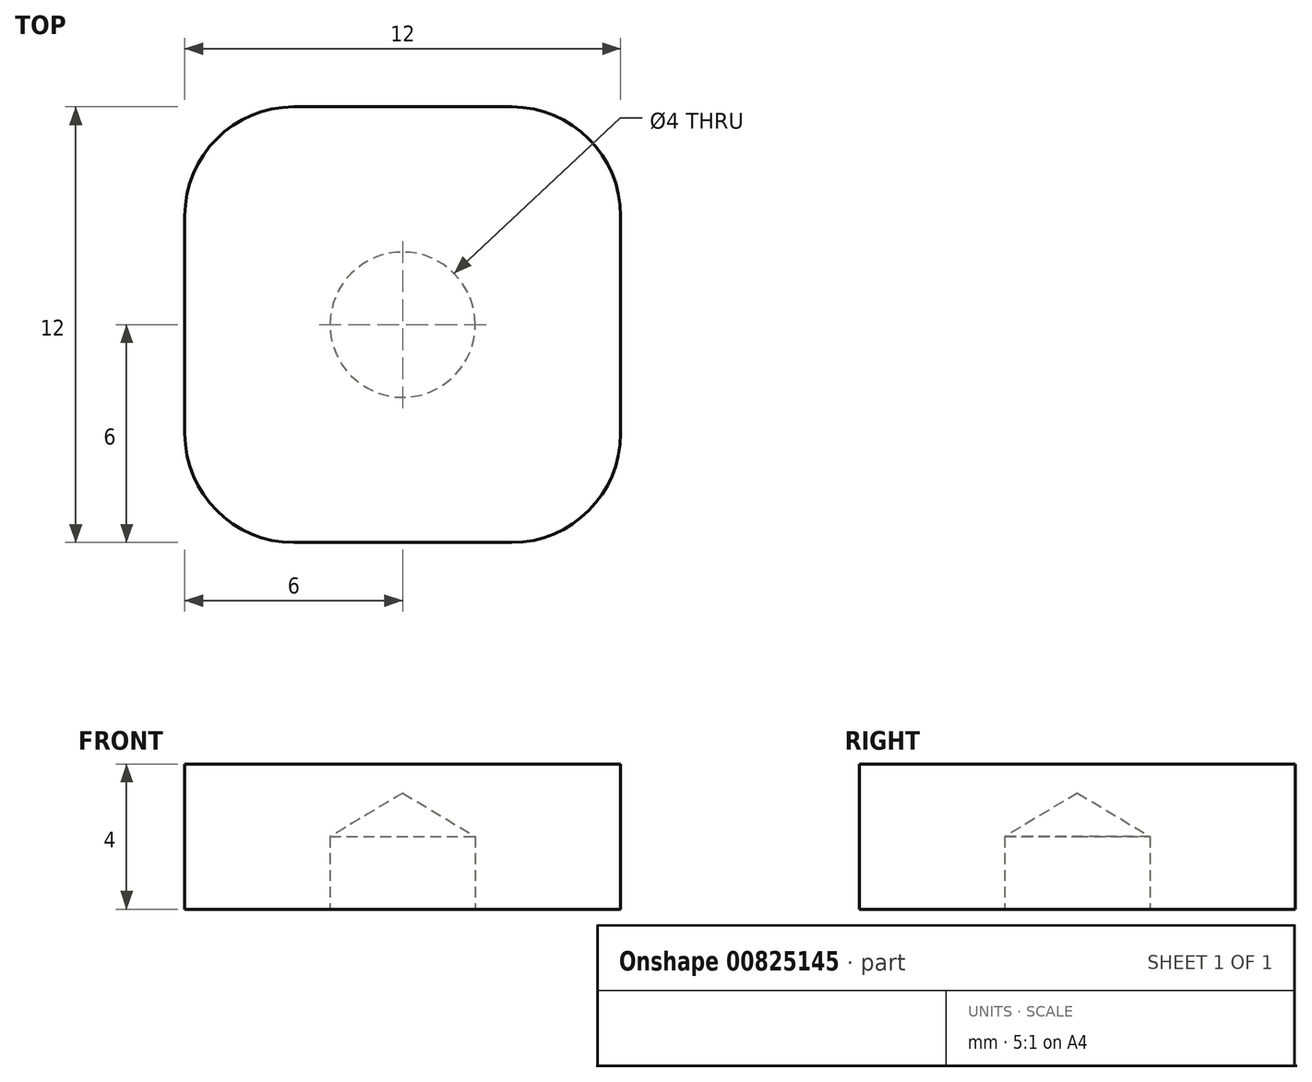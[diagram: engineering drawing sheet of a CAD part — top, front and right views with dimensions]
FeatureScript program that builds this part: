
annotation { "Feature Type Name" : "Feature", "Feature Type Description" : "" }
export const myFeature = defineFeature(function(context is Context, id is Id, definition is map)
    precondition{}
    {
        {
            var Q0;
            Q0=qCreatedBy(makeId("Top.planeOp"),FACE);
            var sketch = newSketch(context, id + "F0", { "sketchPlane" : qUnion([Q0])});
            skLineSegment(sketch, "E0.bottom", {"start": v(-6, 6) * mm, "end": v(6, 6) * mm});
            skLineSegment(sketch, "E0.top", {"start": v(-6, -6) * mm, "end": v(6, -6) * mm});
            skLineSegment(sketch, "E0.left", {"start": v(-6, 6) * mm, "end": v(-6, -6) * mm});
            skLineSegment(sketch, "E0.right", {"start": v(6, 6) * mm, "end": v(6, -6) * mm});
            skPoint(sketch, "E0.middle", {"position": v(0, 0) * mm});
            skLineSegment(sketch, "E1", {"start": v(6, 6) * mm, "end": v(-6, -6) * mm, "construction": true});
            skLineSegment(sketch, "E2", {"start": v(6, -6) * mm, "end": v(-6, 6) * mm, "construction": true});
            skSolve(sketch);
        }
        {
            var Q0;
            Q0=makeQuery(id+"F0.imprint","IMPRINT",FACE,{"disambiguationData":[TD([[makeQuery(id+"F0.imprint","IMPRINT",EDGE,{"derivedFrom":sQuery(id+"F0.wireOp",EDGE,"E0.bottom")}),-1.0]])]});
            extrude(context, id + "F1", {"entities" : qUnion([Q0]), "depth" : 4 * mm, "offsetDistance" : 25 * mm});
        }
        {
            var Q0;
            Q0=sQuery(id+"F0.wireOp",VERTEX,"E0.middle");
            var Q1;
            Q1=makeQuery(id+"F1.opExtrude","SWEPT_BODY",BODY,{"disambiguationData":[OSD([sQuery(id+"F0.wireOp",EDGE,"E0.bottom"),sQuery(id+"F0.wireOp",EDGE,"E0.top"),sQuery(id+"F0.wireOp",EDGE,"E0.left"),sQuery(id+"F0.wireOp",EDGE,"E0.right")])]});
            hole(context, id + "F2", {"style" : HoleStyle.SIMPLE, "endStyle" : HoleEndStyle.BLIND, "oppositeDirection" : true, "holeDiameter" : 4 * mm, "majorDiameter" : 5 * mm, "holeDepth" : 2 * mm, "isTappedThrough" : true, "tappedDepth" : 12 * mm, "tapClearance" : 3, "startFromSketch" : true, "locations" : qUnion([Q0]), "scope" : qUnion([Q1])});
        }
        {
            var Q0;
            Q0=makeQuery(id+"F1.opExtrude","SWEPT_EDGE",EDGE,{"disambiguationData":[OSD([sQuery(id+"F0.wireOp",EDGE,"E0.bottom"),sQuery(id+"F0.wireOp",EDGE,"E0.right")])]});
            var Q1;
            Q1=makeQuery(id+"F1.opExtrude","SWEPT_EDGE",EDGE,{"disambiguationData":[OSD([sQuery(id+"F0.wireOp",EDGE,"E0.bottom"),sQuery(id+"F0.wireOp",EDGE,"E0.left")])]});
            var Q2;
            Q2=makeQuery(id+"F1.opExtrude","SWEPT_EDGE",EDGE,{"disambiguationData":[OSD([sQuery(id+"F0.wireOp",EDGE,"E0.top"),sQuery(id+"F0.wireOp",EDGE,"E0.left")])]});
            var Q3;
            Q3=makeQuery(id+"F1.opExtrude","SWEPT_EDGE",EDGE,{"disambiguationData":[OSD([sQuery(id+"F0.wireOp",EDGE,"E0.top"),sQuery(id+"F0.wireOp",EDGE,"E0.right")])]});
            fillet(context, id + "F3", {"entities" : qUnion([Q0, Q1, Q2, Q3]), "radius" : 3 * mm, "tangentPropagation" : true, "allowEdgeOverflow" : false});
        }
    });
